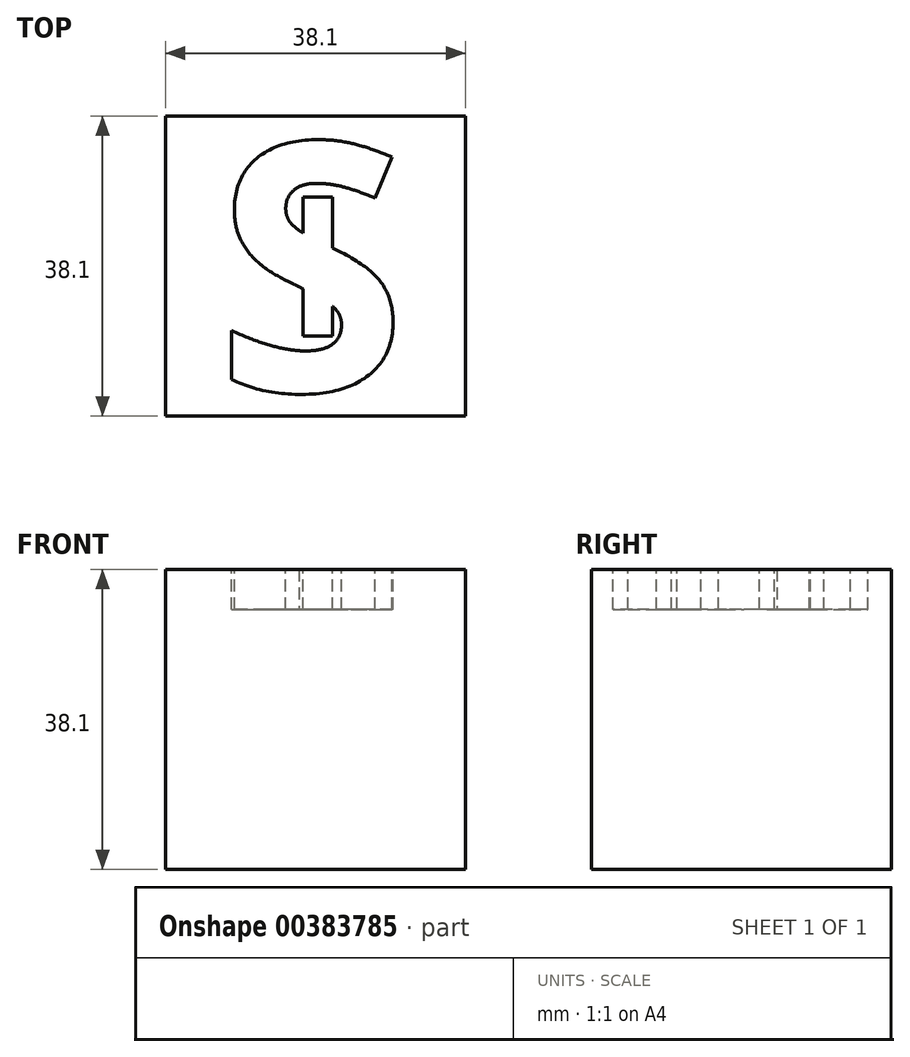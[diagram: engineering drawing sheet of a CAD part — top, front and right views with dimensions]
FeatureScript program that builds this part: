
annotation { "Feature Type Name" : "Feature", "Feature Type Description" : "" }
export const myFeature = defineFeature(function(context is Context, id is Id, definition is map)
    precondition{}
    {
        {
            var Q0;
            Q0=qCreatedBy(makeId("Top.planeOp"),FACE);
            var sketch = newSketch(context, id + "F0", { "sketchPlane" : qUnion([Q0])});
            skLineSegment(sketch, "E0.bottom", {"start": v(-66.7, 43.36) * mm, "end": v(-28.6, 43.36) * mm});
            skLineSegment(sketch, "E0.top", {"start": v(-66.7, 5.26) * mm, "end": v(-28.6, 5.26) * mm});
            skLineSegment(sketch, "E0.left", {"start": v(-66.7, 43.36) * mm, "end": v(-66.7, 5.26) * mm});
            skLineSegment(sketch, "E0.right", {"start": v(-28.6, 43.36) * mm, "end": v(-28.6, 5.26) * mm});
            skPoint(sketch, "E0.middle", {"position": v(-47.66, 24.31) * mm});
            skSolve(sketch);
        }
        {
            var Q0;
            Q0 = qSketchRegion(id + "F0", true);
            extrude(context, id + "F1", {"entities" : qUnion([Q0]), "depth" : 38.1 * mm});
        }
        {
            var Q0;
            Q0=makeQuery(id+"F1.opExtrude","CAP_FACE",FACE,{"disambiguationData":[OSD([sQuery(id+"F0.wireOp",EDGE,"E0.bottom"),sQuery(id+"F0.wireOp",EDGE,"E0.top"),sQuery(id+"F0.wireOp",EDGE,"E0.left"),sQuery(id+"F0.wireOp",EDGE,"E0.right")])],"isStart":false});
            var sketch = newSketch(context, id + "F2", { "sketchPlane" : qUnion([Q0])});
            skText(sketch, "E1", { "text": "S", "fontName": "OpenSans-Bold.ttf"});
            skPoint(sketch, "E2", {"position": v(-47.66, 5.26) * mm});
            skPoint(sketch, "E3", {"position": v(-47.66, 24.31) * mm});
            skPoint(sketch, "E4", {"position": v(-47.66, 43.36) * mm});
            skText(sketch, "E5", { "text": "I", "fontName": "OpenSans-Bold.ttf"});
            const initialGuessF2  = {"E1": [-0.06036, 0.00844, 1, 0, 0.03175], "E5": [-0.05144, 0.01542, 1, 0, 0.01778]};
            skSetInitialGuess(sketch, initialGuessF2);
            skSolve(sketch);
        }
        {
            var Q0;
            Q0 = qSketchRegion(id + "F2", true);
            extrude(context, id + "F3", {"entities" : qUnion([Q0]), "operationType" : NewBodyOperationType.REMOVE, "oppositeDirection" : true, "depth" : 5.08 * mm});
        }
    });
